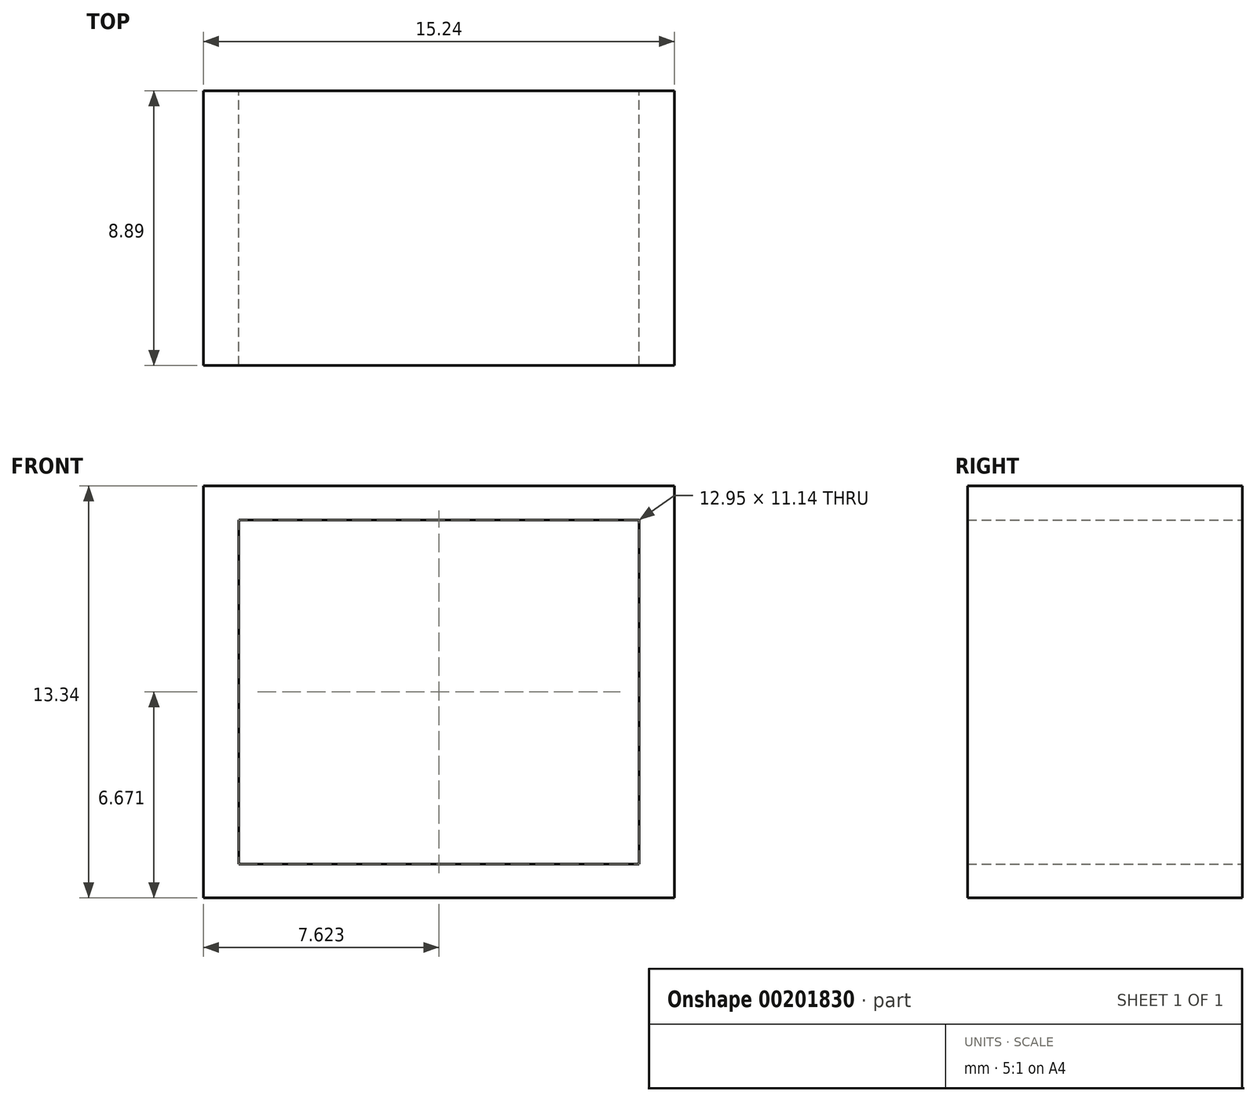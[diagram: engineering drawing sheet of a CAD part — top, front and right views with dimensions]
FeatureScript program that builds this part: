
annotation { "Feature Type Name" : "Feature", "Feature Type Description" : "" }
export const myFeature = defineFeature(function(context is Context, id is Id, definition is map)
    precondition{}
    {
        {
            var Q0;
            Q0=qCreatedBy(makeId("Front.planeOp"),FACE);
            var sketch = newSketch(context, id + "F0", { "sketchPlane" : qUnion([Q0])});
            skLineSegment(sketch, "E0.bottom", {"start": v(-38.09, 17.7) * mm, "end": v(-51.04, 17.7) * mm});
            skLineSegment(sketch, "E0.top", {"start": v(-38.09, 28.83) * mm, "end": v(-51.04, 28.83) * mm});
            skLineSegment(sketch, "E0.left", {"start": v(-38.09, 17.7) * mm, "end": v(-38.09, 28.83) * mm});
            skLineSegment(sketch, "E0.right", {"start": v(-51.04, 17.7) * mm, "end": v(-51.04, 28.83) * mm});
            skPoint(sketch, "E0.middle", {"position": v(-44.57, 23.26) * mm});
            skLineSegment(sketch, "E1.bottom", {"start": v(-36.95, 16.6) * mm, "end": v(-52.19, 16.6) * mm});
            skLineSegment(sketch, "E1.top", {"start": v(-36.95, 29.93) * mm, "end": v(-52.19, 29.93) * mm});
            skLineSegment(sketch, "E1.left", {"start": v(-36.95, 16.6) * mm, "end": v(-36.95, 29.93) * mm});
            skLineSegment(sketch, "E1.right", {"start": v(-52.19, 16.6) * mm, "end": v(-52.19, 29.93) * mm});
            skSolve(sketch);
        }
        {
            var Q0;
            Q0=makeQuery(id+"F0.imprint","IMPRINT",FACE,{"disambiguationData":[TD([[makeQuery(id+"F0.imprint","IMPRINT",EDGE,{"derivedFrom":sQuery(id+"F0.wireOp",EDGE,"E0.bottom")}),1.0]])]});
            extrude(context, id + "F1", {"entities" : qUnion([Q0]), "depth" : 8.9 * mm});
        }
    });
